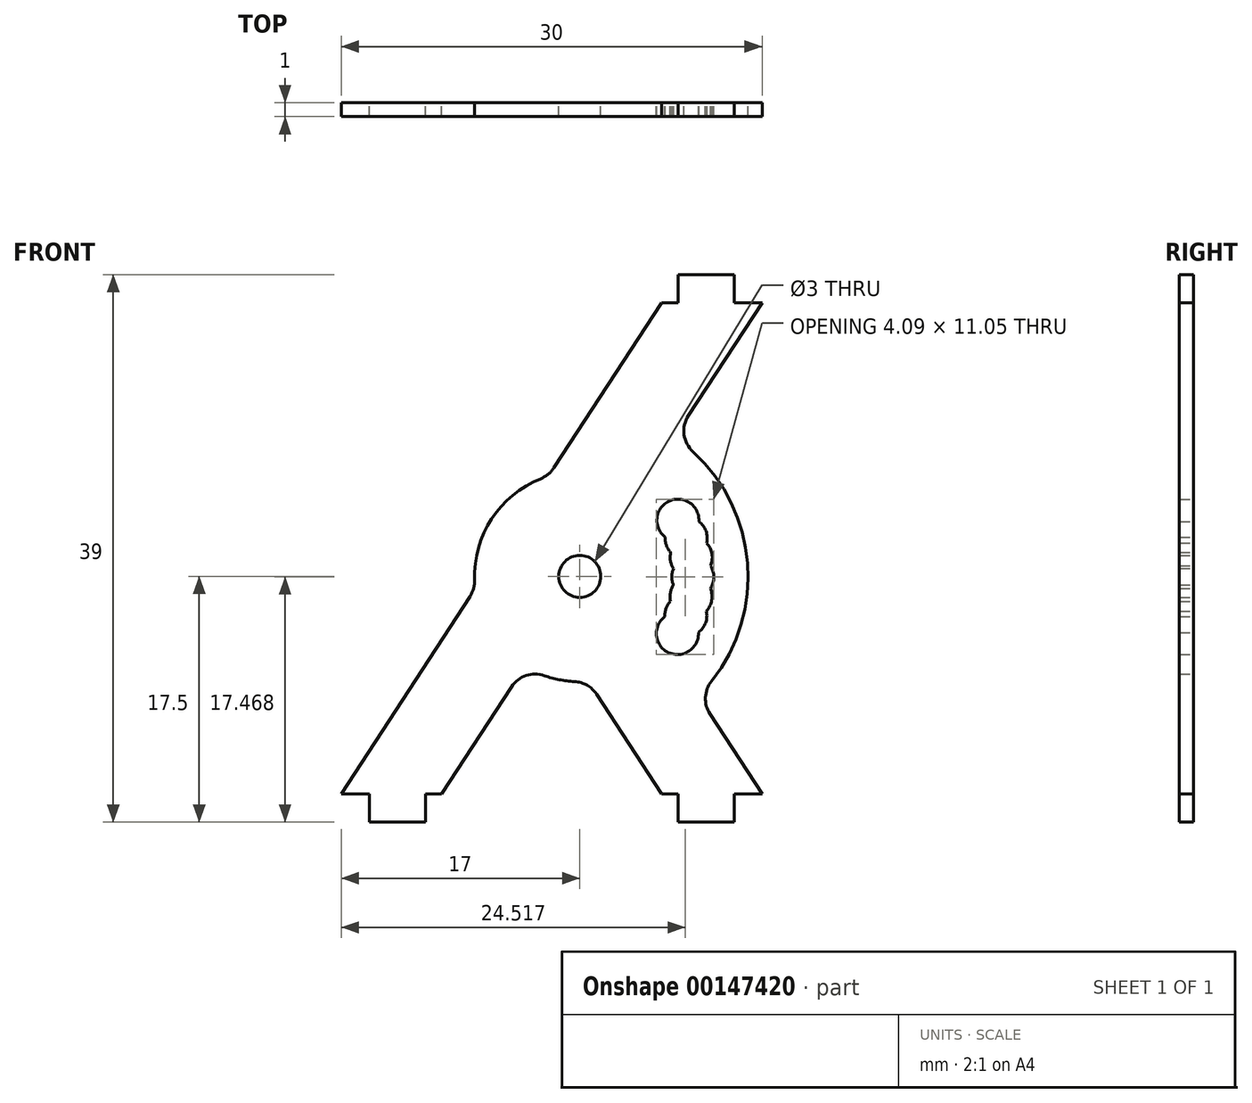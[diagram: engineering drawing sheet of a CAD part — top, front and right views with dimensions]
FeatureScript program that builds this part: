
annotation { "Feature Type Name" : "Feature", "Feature Type Description" : "" }
export const myFeature = defineFeature(function(context is Context, id is Id, definition is map)
    precondition{}
    {
        {
            var Q0;
            Q0=qCreatedBy(makeId("Front.planeOp"),FACE);
            var sketch = newSketch(context, id + "F0", { "sketchPlane" : qUnion([Q0])});
            skLineSegment(sketch, "E0.bottom", {"start": v(7.84, 17.5) * mm, "end": v(9, 17.5) * mm});
            skLineSegment(sketch, "E0.top", {"start": v(-15, -17.5) * mm, "end": v(-13, -17.5) * mm});
            skLineSegment(sketch, "E1", {"start": v(15, 17.5) * mm, "end": v(8.75, 7.92) * mm});
            skLineSegment(sketch, "E2", {"start": v(-15, -17.5) * mm, "end": v(-5.45, -2.86) * mm});
            skLineSegment(sketch, "E3.trimOffspring", {"start": v(-1.9, -8.4) * mm, "end": v(-7.84, -17.5) * mm});
            skLineSegment(sketch, "E4.trimOffspring", {"start": v(2.6, -9.48) * mm, "end": v(7.84, -17.5) * mm});
            skLineSegment(sketch, "E5.trimOffspring", {"start": v(-0.21, 5.17) * mm, "end": v(7.84, 17.5) * mm});
            skLineSegment(sketch, "E6.trimOffspring", {"start": v(10.45, -10.52) * mm, "end": v(15, -17.5) * mm});
            skLineSegment(sketch, "E7.trimOffspring", {"start": v(7.84, -17.5) * mm, "end": v(9, -17.5) * mm});
            skLineSegment(sketch, "E8.top", {"start": v(13, 19.5) * mm, "end": v(9, 19.5) * mm});
            skLineSegment(sketch, "E8.left", {"start": v(13, 17.5) * mm, "end": v(13, 19.5) * mm});
            skLineSegment(sketch, "E8.right", {"start": v(9, 17.5) * mm, "end": v(9, 19.5) * mm});
            skLineSegment(sketch, "E9.top", {"start": v(-13, -19.5) * mm, "end": v(-9, -19.5) * mm});
            skLineSegment(sketch, "E9.left", {"start": v(-13, -17.5) * mm, "end": v(-13, -19.5) * mm});
            skLineSegment(sketch, "E9.right", {"start": v(-9, -17.5) * mm, "end": v(-9, -19.5) * mm});
            skLineSegment(sketch, "E10.top", {"start": v(9, -19.5) * mm, "end": v(13, -19.5) * mm});
            skLineSegment(sketch, "E10.left", {"start": v(9, -17.5) * mm, "end": v(9, -19.5) * mm});
            skLineSegment(sketch, "E10.right", {"start": v(13, -17.5) * mm, "end": v(13, -19.5) * mm});
            skLineSegment(sketch, "E11.trimOffspring", {"start": v(-9, -17.5) * mm, "end": v(-7.84, -17.5) * mm});
            skLineSegment(sketch, "E12.trimOffspring", {"start": v(13, -17.5) * mm, "end": v(15, -17.5) * mm});
            skLineSegment(sketch, "E13.trimOffspring", {"start": v(13, 17.5) * mm, "end": v(15, 17.5) * mm});
            skCircle(sketch, "E14", {"center": v(2, -2) * mm, "radius": 1.5 * mm});
            skArc(sketch, "E15", {"start": v(10.45, -10.52) * mm, "mid": v(13.95, -0.9) * mm, "end": v(8.75, 7.92) * mm});
            skArc(sketch, "E16", {"start": v(-0.21, 5.17) * mm, "mid": v(-4.28, 2.1) * mm, "end": v(-5.45, -2.86) * mm});
            skArc(sketch, "E17.trimOffspring", {"start": v(-1.9, -8.4) * mm, "mid": v(0.26, -9.3) * mm, "end": v(2.6, -9.48) * mm});
            skLineSegment(sketch, "E18", {"start": v(2, -2) * mm, "end": v(14, -2) * mm, "construction": true});
            skLineSegment(sketch, "E19", {"start": v(2, -2) * mm, "end": v(9, 2) * mm, "construction": true});
            skLineSegment(sketch, "E20", {"start": v(2, -2) * mm, "end": v(8.96, -6.06) * mm, "construction": true});
            skArc(sketch, "E21", {"start": v(10.5, 1.92) * mm, "mid": v(8.37, 3.36) * mm, "end": v(8.1, 0.8) * mm});
            skCircle(sketch, "E22", {"center": v(2, -2) * mm, "radius": 8.06 * mm, "construction": true});
            skLineSegment(sketch, "E23", {"start": v(2, -2) * mm, "end": v(9.59, 0.72) * mm, "construction": true});
            skLineSegment(sketch, "E24", {"start": v(2, -2) * mm, "end": v(9.95, -0.64) * mm, "construction": true});
            skLineSegment(sketch, "E25", {"start": v(2, -2) * mm, "end": v(10.06, -2.04) * mm, "construction": true});
            skArc(sketch, "E26", {"start": v(8.68, -1.45) * mm, "mid": v(8.56, -2.03) * mm, "end": v(8.68, -2.61) * mm});
            skArc(sketch, "E27", {"start": v(8.49, -0.3) * mm, "mid": v(8.47, -0.89) * mm, "end": v(8.68, -1.45) * mm});
            skArc(sketch, "E28", {"start": v(8.1, 0.8) * mm, "mid": v(8.18, 0.22) * mm, "end": v(8.49, -0.3) * mm});
            skArc(sketch, "E29.trimOffspring", {"start": v(11.05, 0.38) * mm, "mid": v(11, 1.23) * mm, "end": v(10.5, 1.92) * mm});
            skArc(sketch, "E30.trimOffspring", {"start": v(11.32, -1.23) * mm, "mid": v(11.42, -0.38) * mm, "end": v(11.05, 0.38) * mm});
            skLineSegment(sketch, "E31", {"start": v(2, -2) * mm, "end": v(9.56, -4.8) * mm, "construction": true});
            skLineSegment(sketch, "E32", {"start": v(2, -2) * mm, "end": v(9.93, -3.44) * mm, "construction": true});
            skArc(sketch, "E33", {"start": v(8.47, -3.76) * mm, "mid": v(8.16, -4.27) * mm, "end": v(8.07, -4.86) * mm});
            skArc(sketch, "E34", {"start": v(8.07, -4.86) * mm, "mid": v(8.32, -7.42) * mm, "end": v(10.46, -6) * mm});
            skArc(sketch, "E35.trimOffspring", {"start": v(11.32, -2.86) * mm, "mid": v(11.56, -2.04) * mm, "end": v(11.32, -1.23) * mm});
            skArc(sketch, "E36.trimOffspring", {"start": v(11.03, -4.46) * mm, "mid": v(11.4, -3.7) * mm, "end": v(11.32, -2.86) * mm});
            skArc(sketch, "E37.trimOffspring", {"start": v(10.46, -6) * mm, "mid": v(10.97, -5.31) * mm, "end": v(11.03, -4.46) * mm});
            skArc(sketch, "E38.trimOffspring", {"start": v(8.68, -2.61) * mm, "mid": v(8.46, -3.17) * mm, "end": v(8.47, -3.76) * mm});
            skSolve(sketch);
        }
        {
            var Q0;
            Q0 = qSketchRegion(id + "F0", true);
            extrude(context, id + "F1", {"entities" : qUnion([Q0]), "depth" : 1 * mm});
        }
        {
            var Q0;
            Q0=makeQuery(id+"F1.opExtrude","SWEPT_EDGE",EDGE,{"disambiguationData":[OSD([sQuery(id+"F0.wireOp",EDGE,"E3.trimOffspring"),sQuery(id+"F0.wireOp",EDGE,"E17.trimOffspring")])]});
            var Q1;
            Q1=makeQuery(id+"F1.opExtrude","SWEPT_EDGE",EDGE,{"disambiguationData":[OSD([sQuery(id+"F0.wireOp",EDGE,"E4.trimOffspring"),sQuery(id+"F0.wireOp",EDGE,"E17.trimOffspring")])]});
            var Q2;
            Q2=makeQuery(id+"F1.opExtrude","SWEPT_EDGE",EDGE,{"disambiguationData":[OSD([sQuery(id+"F0.wireOp",EDGE,"E6.trimOffspring"),sQuery(id+"F0.wireOp",EDGE,"E15")])]});
            var Q3;
            Q3=makeQuery(id+"F1.opExtrude","SWEPT_EDGE",EDGE,{"disambiguationData":[OSD([sQuery(id+"F0.wireOp",EDGE,"E1"),sQuery(id+"F0.wireOp",EDGE,"E15")])]});
            var Q4;
            Q4=makeQuery(id+"F1.opExtrude","SWEPT_EDGE",EDGE,{"disambiguationData":[OSD([sQuery(id+"F0.wireOp",EDGE,"E5.trimOffspring"),sQuery(id+"F0.wireOp",EDGE,"E16")])]});
            var Q5;
            Q5=makeQuery(id+"F1.opExtrude","SWEPT_EDGE",EDGE,{"disambiguationData":[OSD([sQuery(id+"F0.wireOp",EDGE,"E2"),sQuery(id+"F0.wireOp",EDGE,"E16")])]});
            fillet(context, id + "F2", {"entities" : qUnion([Q0, Q1, Q2, Q3, Q4, Q5]), "radius" : 2 * mm, "tangentPropagation" : true, "allowEdgeOverflow" : false});
        }
    });
